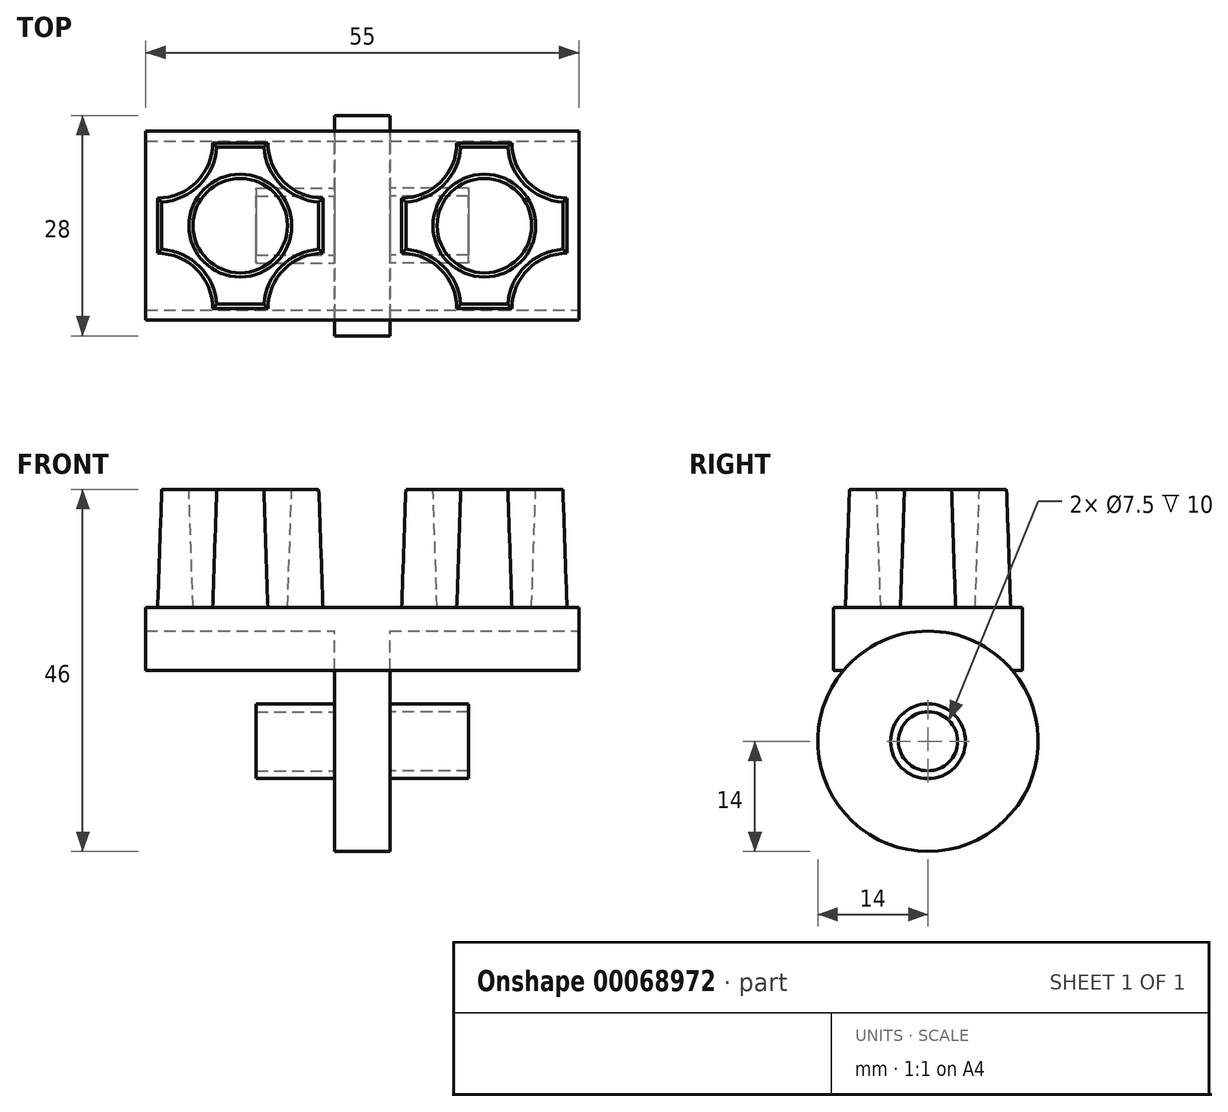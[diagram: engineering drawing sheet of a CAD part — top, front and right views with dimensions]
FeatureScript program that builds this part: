
annotation { "Feature Type Name" : "Feature", "Feature Type Description" : "" }
export const myFeature = defineFeature(function(context is Context, id is Id, definition is map)
    precondition{}
    {
        {
            var Q0;
            Q0=qCreatedBy(makeId("Top.planeOp"),FACE);
            var sketch = newSketch(context, id + "F0", { "sketchPlane" : qUnion([Q0])});
            skLineSegment(sketch, "E0.rect.bottom", {"start": v(27.5, -12) * mm, "end": v(-27.5, -12) * mm});
            skLineSegment(sketch, "E0.rect.top", {"start": v(27.5, 12) * mm, "end": v(-27.5, 12) * mm});
            skLineSegment(sketch, "E0.rect.left", {"start": v(27.5, -12) * mm, "end": v(27.5, 12) * mm});
            skLineSegment(sketch, "E0.rect.right", {"start": v(-27.5, -12) * mm, "end": v(-27.5, 12) * mm});
            skPoint(sketch, "E0.rect.middle", {"position": v(0, 0) * mm});
            skSolve(sketch);
        }
        {
            var Q0;
            Q0=makeQuery(id+"F0.imprint","IMPRINT",FACE,{"disambiguationData":[TD([[makeQuery(id+"F0.imprint","IMPRINT",EDGE,{"derivedFrom":sQuery(id+"F0.wireOp",EDGE,"E0.rect.bottom")}),-1.0]])]});
            extrude(context, id + "F1", {"entities" : qUnion([Q0]), "depth" : 8 * mm});
        }
        {
            var Q0;
            Q0=makeQuery(id+"F1.opExtrude","SWEPT_FACE",FACE,{"disambiguationData":[OSD([sQuery(id+"F0.wireOp",EDGE,"E0.rect.left")])]});
            var sketch = newSketch(context, id + "F2", { "sketchPlane" : qUnion([Q0])});
            skCircle(sketch, "E1", {"center": v(0, -9) * mm, "radius": 14 * mm});
            skSolve(sketch);
        }
        {
            var Q0;
            {var subQ0=sQuery(id+"F2.wireOp",EDGE,"E1");var subQ1=makeQuery(id+"F1.opExtrude","CAP_EDGE",EDGE,{"disambiguationData":[OSD([sQuery(id+"F0.wireOp",EDGE,"E0.rect.left")])],"isStart":true});var subQ2=makeQuery(id+"F2.imprint","INTERSECT",VERTEX,{"disambiguationData":[OD(0.0)],"derivedFrom":[subQ1,subQ0]});Q0=makeQuery(id+"F2.imprint","IMPRINT",FACE,{"disambiguationData":[TD([[makeQuery(id+"F2.imprint","IMPRINT",EDGE,{"disambiguationData":[TD([[subQ2,1.0]])],"derivedFrom":subQ0}),1.0]])]});}
            extrude(context, id + "F3", {"entities" : qUnion([Q0]), "operationType" : NewBodyOperationType.REMOVE, "oppositeDirection" : true, "depth" : 60 * mm});
        }
        {
            var Q0;
            Q0=qCreatedBy(makeId("Right.planeOp"),FACE);
            var sketch = newSketch(context, id + "F4", { "sketchPlane" : qUnion([Q0])});
            skCircle(sketch, "E2", {"center": v(0, -9) * mm, "radius": 14 * mm});
            skSolve(sketch);
        }
        {
            var Q0;
            Q0=makeQuery(id+"F4.imprint","IMPRINT",FACE,{"disambiguationData":[TD([[makeQuery(id+"F4.imprint","IMPRINT",EDGE,{"derivedFrom":sQuery(id+"F4.wireOp",EDGE,"E2")}),1.0]])]});
            extrude(context, id + "F5", {"entities" : qUnion([Q0]), "operationType" : NewBodyOperationType.ADD, "depth" : 3.5 * mm, "hasSecondDirection" : true, "secondDirectionOppositeDirection" : true, "secondDirectionDepth" : 3.5 * mm});
        }
        {
            var Q0;
            Q0=makeQuery(id+"F5.opExtrude","CAP_FACE",FACE,{"disambiguationData":[OSD([sQuery(id+"F4.wireOp",EDGE,"E2")])],"isStart":false});
            var sketch = newSketch(context, id + "F6", { "sketchPlane" : qUnion([Q0])});
            skCircle(sketch, "E3", {"center": v(0, -9) * mm, "radius": 4.75 * mm});
            skCircle(sketch, "E4", {"center": v(0, -9) * mm, "radius": 3.75 * mm});
            skSolve(sketch);
        }
        {
            var Q0;
            Q0=makeQuery(id+"F6.imprint","IMPRINT",FACE,{"disambiguationData":[TD([[makeQuery(id+"F6.imprint","IMPRINT",EDGE,{"derivedFrom":sQuery(id+"F6.wireOp",EDGE,"E3")}),1.0]])]});
            extrude(context, id + "F7", {"entities" : qUnion([Q0]), "operationType" : NewBodyOperationType.ADD, "depth" : 10 * mm});
        }
        {
            var Q0;
            Q0=makeQuery(id+"F1.opExtrude","SWEPT_BODY",BODY,{"disambiguationData":[OSD([sQuery(id+"F0.wireOp",EDGE,"E0.rect.bottom"),sQuery(id+"F0.wireOp",EDGE,"E0.rect.top"),sQuery(id+"F0.wireOp",EDGE,"E0.rect.left"),sQuery(id+"F0.wireOp",EDGE,"E0.rect.right")])]});
            var Q1;
            Q1=qCreatedBy(makeId("Right.planeOp"),FACE);
            mirror(context, id + "F8", {"operationType" : NewBodyOperationType.ADD, "entities" : qUnion([Q0]), "mirrorPlane" : qUnion([Q1])});
        }
        {
            var Q0;
            Q0=makeQuery(id+"F1.opExtrude","CAP_FACE",FACE,{"disambiguationData":[OSD([sQuery(id+"F0.wireOp",EDGE,"E0.rect.bottom"),sQuery(id+"F0.wireOp",EDGE,"E0.rect.top"),sQuery(id+"F0.wireOp",EDGE,"E0.rect.left"),sQuery(id+"F0.wireOp",EDGE,"E0.rect.right")])],"isStart":false});
            var sketch = newSketch(context, id + "F9", { "sketchPlane" : qUnion([Q0])});
            skLineSegment(sketch, "E5.rect.bottom", {"start": v(12, 10.5) * mm, "end": v(19, 10.5) * mm});
            skLineSegment(sketch, "E5.rect.top", {"start": v(12, -10.5) * mm, "end": v(19, -10.5) * mm});
            skLineSegment(sketch, "E5.rect.left", {"start": v(5, 3.5) * mm, "end": v(5, -3.5) * mm});
            skLineSegment(sketch, "E5.rect.right", {"start": v(26, 3.5) * mm, "end": v(26, -3.5) * mm});
            skPoint(sketch, "E5.rect.middle", {"position": v(15.5, 0) * mm});
            skArc(sketch, "E6", {"start": v(26, -3.5) * mm, "mid": v(21.05, -5.55) * mm, "end": v(19, -10.5) * mm});
            skArc(sketch, "E7", {"start": v(19, 10.5) * mm, "mid": v(21.05, 5.55) * mm, "end": v(26, 3.5) * mm});
            skArc(sketch, "E8", {"start": v(5, 3.5) * mm, "mid": v(9.95, 5.55) * mm, "end": v(12, 10.5) * mm});
            skArc(sketch, "E9", {"start": v(12, -10.5) * mm, "mid": v(9.95, -5.55) * mm, "end": v(5, -3.5) * mm});
            skCircle(sketch, "E10", {"center": v(15.5, 0) * mm, "radius": 6 * mm});
            skSolve(sketch);
        }
        {
            var Q0;
            Q0=makeQuery(id+"F9.imprint","IMPRINT",FACE,{"disambiguationData":[TD([[makeQuery(id+"F9.imprint","IMPRINT",EDGE,{"derivedFrom":sQuery(id+"F9.wireOp",EDGE,"E5.rect.bottom")}),-1.0]])]});
            extrude(context, id + "F10", {"entities" : qUnion([Q0]), "depth" : 15 * mm, "hasDraft" : true, "draftAngle" : 2 * degree, "draftPullDirection" : true});
        }
        {
            var Q0;
            Q0=makeQuery(id+"F10.opExtrude","SWEPT_BODY",BODY,{"disambiguationData":[OSD([sQuery(id+"F9.wireOp",EDGE,"E5.rect.bottom"),sQuery(id+"F9.wireOp",EDGE,"E5.rect.top"),sQuery(id+"F9.wireOp",EDGE,"E5.rect.left"),sQuery(id+"F9.wireOp",EDGE,"E5.rect.right"),sQuery(id+"F9.wireOp",EDGE,"E6"),sQuery(id+"F9.wireOp",EDGE,"E7"),sQuery(id+"F9.wireOp",EDGE,"E8"),sQuery(id+"F9.wireOp",EDGE,"E9"),sQuery(id+"F9.wireOp",EDGE,"E10")])]});
            var Q1;
            Q1=qCreatedBy(makeId("Right.planeOp"),FACE);
            mirror(context, id + "F11", {"operationType" : NewBodyOperationType.ADD, "entities" : qUnion([Q0]), "mirrorPlane" : qUnion([Q1])});
        }
    });
